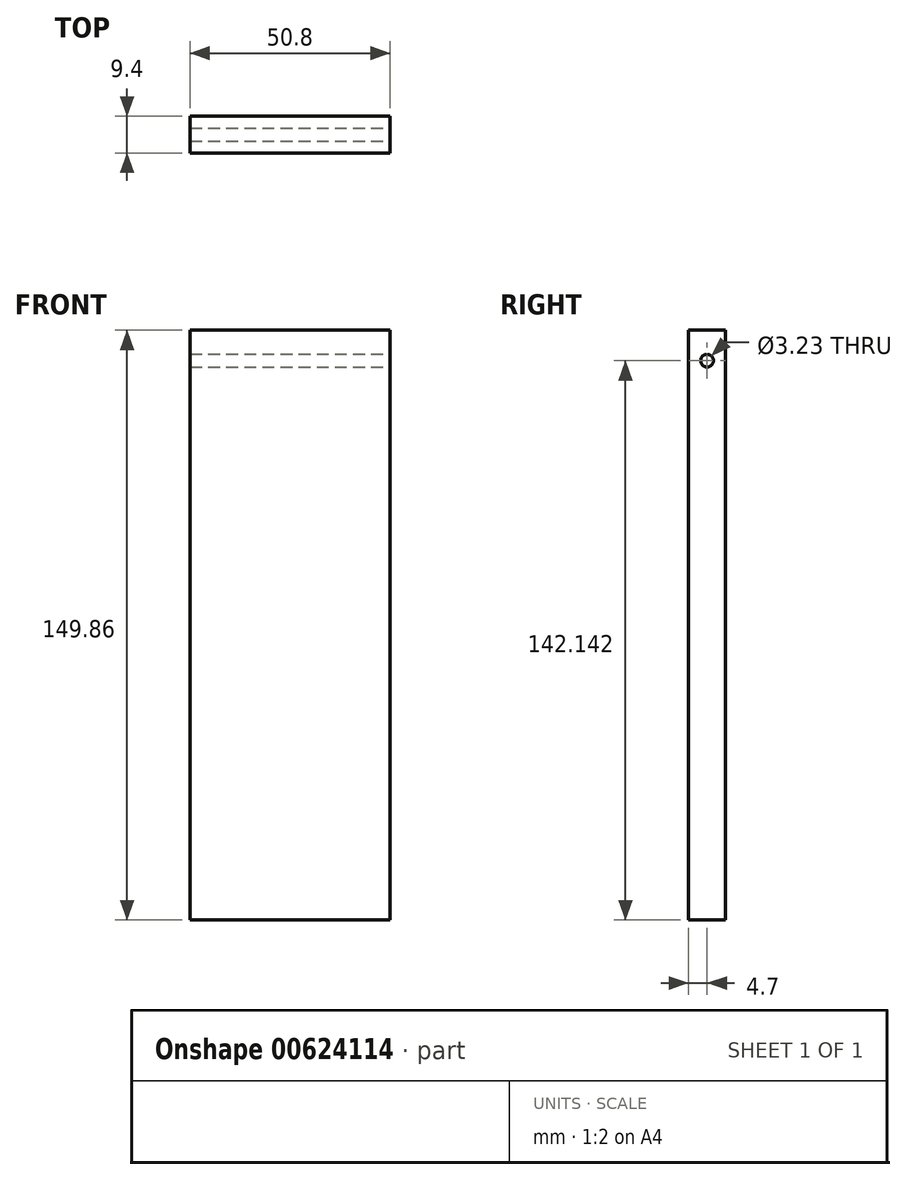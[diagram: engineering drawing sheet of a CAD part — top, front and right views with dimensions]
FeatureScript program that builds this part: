
annotation { "Feature Type Name" : "Feature", "Feature Type Description" : "" }
export const myFeature = defineFeature(function(context is Context, id is Id, definition is map)
    precondition{}
    {
        {
            var Q0;
            Q0=qCreatedBy(makeId("Front.planeOp"),FACE);
            var sketch = newSketch(context, id + "F0", { "sketchPlane" : qUnion([Q0])});
            skLineSegment(sketch, "E0.bottom", {"start": v(-53.63, 109.56) * mm, "end": v(-2.83, 109.56) * mm});
            skLineSegment(sketch, "E0.top", {"start": v(-53.63, -40.3) * mm, "end": v(-2.83, -40.3) * mm});
            skLineSegment(sketch, "E0.left", {"start": v(-53.63, 109.56) * mm, "end": v(-53.63, -40.3) * mm});
            skLineSegment(sketch, "E0.right", {"start": v(-2.83, 109.56) * mm, "end": v(-2.83, -40.3) * mm});
            skSolve(sketch);
        }
        {
            var Q0;
            Q0 = qSketchRegion(id + "F0", true);
            extrude(context, id + "F1", {"entities" : qUnion([Q0]), "endBound" : BoundingType.SYMMETRIC, "depth" : 9.4 * mm, "offsetDistance" : 25.4 * mm});
        }
        {
            var Q0;
            Q0=makeQuery(id+"F1.opExtrude","SWEPT_FACE",FACE,{"disambiguationData":[OSD([sQuery(id+"F0.wireOp",EDGE,"E0.right")])]});
            var sketch = newSketch(context, id + "F2", { "sketchPlane" : qUnion([Q0])});
            skCircle(sketch, "E1", {"center": v(0, 101.84) * mm, "radius": 1.61 * mm});
            skPoint(sketch, "E1.centerSnap0", {"position": v(0, 109.56) * mm});
            skSolve(sketch);
        }
        {
            var Q0;
            Q0 = qSketchRegion(id + "F2", true);
            extrude(context, id + "F3", {"entities" : qUnion([Q0]), "operationType" : NewBodyOperationType.REMOVE, "oppositeDirection" : true, "depth" : 89.4 * mm, "offsetDistance" : 25.4 * mm});
        }
    });
